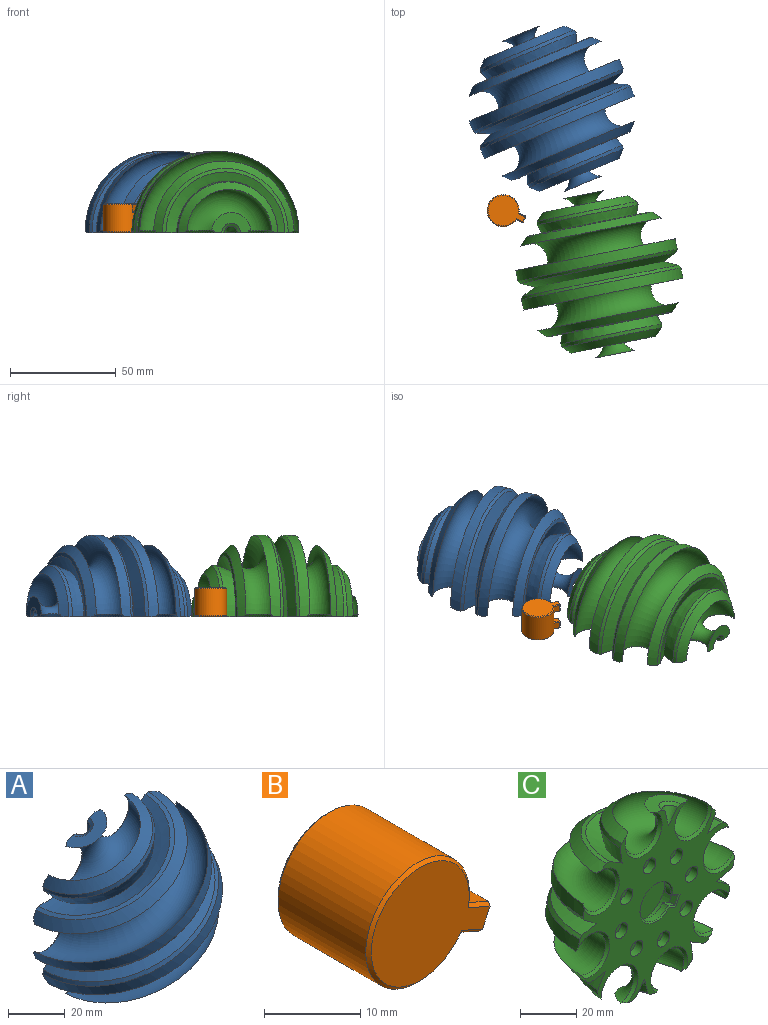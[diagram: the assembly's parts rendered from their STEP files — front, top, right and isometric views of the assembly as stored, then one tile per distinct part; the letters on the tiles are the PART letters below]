
ASSEMBLY  parts=3 mates=2
PART A: 64 faces, bbox 92.5x49.9x87.6 mm
  f0: torus R=12.63mm, axis (-0.38,0,0.92), area 20.6mm2, adj f1,f21,f22
  f1: cone r=3.5mm half-angle=24.8deg, axis (0.38,0,-0.92), area 0.6mm2, adj f0,f22,f59
  f2: plane 17.7x9.72mm, normal (0.38,0,-0.92), area 108.9mm2, adj f3,f22,f50,f51,f59
  f3: torus R=12.81mm, axis (-0.38,0,0.92), area 1353.3mm2, adj f2,f4,f50,f51
  f4: cone r=20.48mm half-angle=45deg, axis (-0.38,0,0.92), area 350.6mm2, adj f3,f22,f50,f51,f61
  f5: cone r=24.75mm half-angle=20.2deg, axis (0.38,0,-0.92), area 533.9mm2, adj f6,f22,f61
  f6: cone r=29.7mm half-angle=69.8deg, axis (0.38,0,-0.92), area 584.1mm2, adj f5,f22,f60
  f7: cone r=29.7mm half-angle=45deg, axis (-0.38,0,0.92), area 508mm2, adj f8,f22,f49,f52,f60
  f8: torus R=30.92mm, axis (-0.38,0,0.92), area 3393.7mm2, adj f7,f9,f49,f52
  f9: cylinder r=38.5mm len=73.07mm, axis (-0.38,0,0.92), area 608mm2, adj f8,f22,f49,f52,f63
  f10: cone r=38.5mm half-angle=65.2deg, axis (0.38,0,-0.92), area 790.5mm2, adj f11,f22,f63
  f11: cone r=38.5mm half-angle=65.2deg, axis (-0.38,0,0.92), area 790.5mm2, adj f10,f22,f62
  f12: cylinder r=38.5mm len=73.07mm, axis (-0.38,0,0.92), area 608mm2, adj f13,f22,f48,f53,f62
  f13: torus R=30.92mm, axis (-0.38,0,0.92), area 3395.4mm2, adj f12,f14,f48,f53
  f14: cone r=33.97mm half-angle=45deg, axis (0.38,0,-0.92), area 508mm2, adj f13,f22,f48,f53,f58
  f15: cone r=29.7mm half-angle=69.8deg, axis (-0.38,0,0.92), area 584.1mm2, adj f16,f22,f58
  f16: cone r=24.75mm half-angle=20.2deg, axis (-0.38,0,0.92), area 533.9mm2, adj f15,f22,f57
  f17: cone r=24.75mm half-angle=45deg, axis (0.38,0,-0.92), area 350.7mm2, adj f18,f22,f54,f55,f57
  f18: torus R=12.81mm, axis (-0.38,0,0.92), area 1355.2mm2, adj f17,f19,f54,f55
  f19: plane 17.7x9.72mm, normal (-0.38,0,0.92), area 108.9mm2, adj f18,f22,f54,f55,f56
  f20: cone r=3.5mm half-angle=24.8deg, axis (-0.38,0,0.92), area 35.5mm2, adj f22,f56
  f21: cone r=1.93mm half-angle=24.8deg, axis (0.38,0,-0.92), area 9.3mm2, adj f0,f22
  f22: plane 81.31x81.3mm, normal (0,1,0), area 2232.2mm2, adj f0,f1,f2,f4,f5,f6,f7,f9
  f23: cylinder r=3.15mm len=6.3mm, axis (0,1,0), area 66.3mm2, adj f22,f24
  f24: plane 6.3x6.3mm, normal (0,1,0), area 31.2mm2, adj f23
  f25: cylinder r=3.15mm len=6.3mm, axis (0,1,0), area 66.3mm2, adj f22,f26
  f26: plane 6.3x6.3mm, normal (0,1,0), area 31.2mm2, adj f25
  f27: cylinder r=3.15mm len=6.3mm, axis (0,1,0), area 66.3mm2, adj f22,f28
  f28: plane 6.3x6.3mm, normal (0,1,0), area 31.2mm2, adj f27
  f29: cylinder r=3.15mm len=6.3mm, axis (0,1,0), area 66.3mm2, adj f22,f30
  f30: plane 6.3x6.3mm, normal (0,1,0), area 31.2mm2, adj f29
  f31: cylinder r=3.15mm len=6.3mm, axis (0,1,0), area 66.3mm2, adj f22,f32
  f32: plane 6.3x6.3mm, normal (0,1,0), area 31.2mm2, adj f31
  f33: cylinder r=3.15mm len=6.3mm, axis (0,1,0), area 66.3mm2, adj f22,f34
  f34: plane 6.3x6.3mm, normal (0,1,0), area 31.2mm2, adj f33
  f35: cylinder r=3.15mm len=6.3mm, axis (0,1,0), area 66.3mm2, adj f22,f36
  f36: plane 6.3x6.3mm, normal (0,1,0), area 31.2mm2, adj f35
  f37: cylinder r=3.15mm len=6.3mm, axis (0,1,0), area 66.3mm2, adj f22,f38
  f38: plane 6.3x6.3mm, normal (0,1,0), area 31.2mm2, adj f37
  f39: plane 7.15x3.45mm, normal (-0.42,0,-0.91), area 11.2mm2, adj f22,f40,f42,f43,f44,f45,f47
  f40: cylinder r=7.8mm len=15.6mm, axis (0,1,0), area 105.7mm2, adj f39,f41,f44,f45
  f41: plane 3.29x2.85mm, normal (0.42,0,0.91), area 10.2mm2, adj f22,f40,f42,f44,f45
  f42: plane 7.15x3.64mm, normal (-0.91,0,0.42), area 14.3mm2, adj f22,f39,f41,f43,f46,f47
  f43: plane 22.71x22.71mm, normal (0,1,0), area 405.1mm2, adj f39,f42,f47
  f44: cone r=8.3mm half-angle=45deg, axis (0,1,0), area 32.9mm2, adj f22,f39,f40,f41
  f45: plane 22.71x22.71mm, normal (0,-1,0), area 199.5mm2, adj f39,f40,f41,f47
  f46: plane 3.02x1.39mm, normal (0,-1,0), area 0.3mm2, adj f42,f47
  f47: cylinder r=11.35mm len=22.71mm, axis (0,1,0), area 303.8mm2, adj f39,f42,f43,f45,f46
  f48: bspline ~18.61x18.6mm, area 55.9mm2, adj f12,f13,f14,f22
  f49: bspline ~18.57x17.08mm, area 55.8mm2, adj f7,f8,f9,f22
  f50: bspline ~18.69x18.61mm, area 57.5mm2, adj f2,f3,f4,f22
  f51: bspline ~18.66x17.09mm, area 57.5mm2, adj f2,f3,f4,f22
  f52: bspline ~18.51x18.5mm, area 55.9mm2, adj f7,f8,f9,f22
  f53: bspline ~18.5x15.69mm, area 55.9mm2, adj f12,f13,f14,f22
  f54: bspline ~18.69x18.61mm, area 57.5mm2, adj f17,f18,f19,f22
  f55: bspline ~18.66x17.09mm, area 57.5mm2, adj f17,f18,f19,f22
  f56: cone r=3.08mm half-angle=57.4deg, axis (-0.38,0,0.92), area 20.1mm2, adj f19,f20,f22
  f57: cone r=24.04mm half-angle=12.4deg, axis (0.38,0,-0.92), area 128.2mm2, adj f16,f17,f22
  f58: cone r=28.76mm half-angle=77.6deg, axis (0.38,0,-0.92), area 156.6mm2, adj f14,f15,f22
  f59: cone r=4.5mm half-angle=57.4deg, axis (0.38,0,-0.92), area 20.1mm2, adj f1,f2,f22
  f60: cone r=30.41mm half-angle=77.6deg, axis (-0.38,0,0.92), area 156.6mm2, adj f6,f7,f22
  f61: cone r=24.4mm half-angle=12.4deg, axis (-0.38,0,0.92), area 128.2mm2, adj f4,f5,f22
  f62: cone r=38.5mm half-angle=32.6deg, axis (-0.38,0,0.92), area 201.4mm2, adj f11,f12,f22
  f63: cone r=37.59mm half-angle=32.6deg, axis (0.38,0,-0.92), area 201.4mm2, adj f9,f10,f22
PART B: 37 faces, bbox 18.2x13.7x15.2 mm
  f0: cylinder r=7.6mm len=15.2mm, axis (0,1,0), area 591.6mm2, adj f4,f5,f6,f7,f9,f10,f11,f18
  f1: plane 17.45x14.4mm, normal (0,-1,0), area 171.6mm2, adj f24,f25,f26,f27
  f2: plane 17.45x14.4mm, normal (0,1,0), area 171.6mm2, adj f11,f12,f13,f14
  f3: plane 3.2x2.36mm, normal (0.91,0,-0.42), area 8.3mm2, adj f26,f31,f32,f36
  f4: plane 3.2x2.92mm, normal (0.42,0,0.91), area 10.3mm2, adj f0,f27,f32,f33
  f5: plane 3.2x2.78mm, normal (-0.42,0,-0.91), area 9.8mm2, adj f0,f25,f30,f31
  f6: plane 3.81x3.66mm, normal (0,1,0), area 7.7mm2, adj f0,f30,f33,f36
  f7: plane 3.2x2.92mm, normal (0.42,0,0.91), area 10.3mm2, adj f0,f13,f19,f20
  f8: plane 3.2x2.36mm, normal (0.91,0,-0.42), area 8.3mm2, adj f14,f17,f20,f23
  f9: plane 3.2x2.78mm, normal (-0.42,0,-0.91), area 9.8mm2, adj f0,f12,f17,f18
  f10: plane 3.81x3.66mm, normal (0,-1,0), area 7.7mm2, adj f0,f18,f19,f23
  f11: cone r=7.6mm half-angle=45deg, axis (0,-1,0), area 24.6mm2, adj f0,f2,f12,f13
  f12: plane 3.09x1.79mm, normal (-0.29,0.71,-0.64), area 1.8mm2, adj f2,f9,f11,f15
  f13: plane 3.37x1.71mm, normal (0.29,0.71,0.64), area 1.9mm2, adj f2,f7,f11,f16
  f14: plane 2.53x1.45mm, normal (0.64,0.71,-0.29), area 1.5mm2, adj f2,f8,f15,f16
  f15: plane 0.53x0.4mm, normal (0.28,0.58,-0.77), area 0.1mm2, adj f12,f14,f17
  f16: plane 0.53x0.4mm, normal (0.77,0.58,0.28), area 0.1mm2, adj f13,f14,f20
  f17: plane 3.2x0.53mm, normal (0.35,0,-0.94), area 1.8mm2, adj f8,f9,f15,f21
  f18: plane 2.94x1.61mm, normal (-0.29,-0.71,-0.64), area 1.7mm2, adj f0,f9,f10,f21
  f19: plane 2.99x1.7mm, normal (0.29,-0.71,0.64), area 1.8mm2, adj f0,f7,f10,f22
  f20: plane 3.2x0.53mm, normal (0.94,0,0.35), area 1.8mm2, adj f7,f8,f16,f22
  f21: plane 0.53x0.4mm, normal (0.28,-0.58,-0.77), area 0.1mm2, adj f17,f18,f23
  f22: plane 0.53x0.4mm, normal (0.77,-0.58,0.28), area 0.1mm2, adj f19,f20,f23
  f23: plane 2.53x1.45mm, normal (0.64,-0.71,-0.29), area 1.5mm2, adj f8,f10,f21,f22
  f24: cone r=7.2mm half-angle=45deg, axis (0,1,0), area 24.6mm2, adj f0,f1,f25,f27
  f25: plane 3.09x1.79mm, normal (-0.29,-0.71,-0.64), area 1.8mm2, adj f1,f5,f24,f28
  f26: plane 2.53x1.45mm, normal (0.64,-0.71,-0.29), area 1.5mm2, adj f1,f3,f28,f29
  f27: plane 3.37x1.71mm, normal (0.29,-0.71,0.64), area 1.9mm2, adj f1,f4,f24,f29
  f28: plane 0.53x0.4mm, normal (0.28,-0.58,-0.77), area 0.1mm2, adj f25,f26,f31
  f29: plane 0.53x0.4mm, normal (0.77,-0.58,0.28), area 0.1mm2, adj f26,f27,f32
  f30: plane 2.94x1.61mm, normal (-0.29,0.71,-0.64), area 1.7mm2, adj f0,f5,f6,f34
  f31: plane 3.2x0.53mm, normal (0.35,0,-0.94), area 1.8mm2, adj f3,f5,f28,f34
  f32: plane 3.2x0.53mm, normal (0.94,0,0.35), area 1.8mm2, adj f3,f4,f29,f35
  f33: plane 2.99x1.7mm, normal (0.29,0.71,0.64), area 1.8mm2, adj f0,f4,f6,f35
  f34: plane 0.53x0.4mm, normal (0.28,0.58,-0.77), area 0.1mm2, adj f30,f31,f36
  f35: plane 0.53x0.4mm, normal (0.77,0.58,0.28), area 0.1mm2, adj f32,f33,f36
  f36: plane 2.53x1.45mm, normal (0.64,0.71,-0.29), area 1.5mm2, adj f3,f6,f34,f35
PART C: 65 faces, bbox 92.5x46.8x87.3 mm
  f0: cone r=3.5mm half-angle=24.8deg, axis (-0.2,0,-0.98), area 35.5mm2, adj f1,f36
  f1: cone r=3.08mm half-angle=57.4deg, axis (-0.2,0,-0.98), area 20.1mm2, adj f0,f2,f36
  f2: plane 18.78x9.72mm, normal (-0.2,0,-0.98), area 108.9mm2, adj f1,f3,f34,f35,f36
  f3: bspline ~18.66x17.95mm, area 57.5mm2, adj f2,f4,f34,f36
  f4: cone r=20.48mm half-angle=45deg, axis (0.2,0,0.98), area 350.6mm2, adj f3,f5,f34,f35,f36
  f5: cone r=24.04mm half-angle=12.4deg, axis (0.2,0,0.98), area 128.2mm2, adj f4,f6,f36
  f6: cone r=24.75mm half-angle=20.2deg, axis (-0.2,0,-0.98), area 533.9mm2, adj f5,f7,f36
  f7: cone r=29.7mm half-angle=69.8deg, axis (-0.2,0,-0.98), area 584.1mm2, adj f6,f8,f36
  f8: cone r=28.76mm half-angle=77.6deg, axis (0.2,0,0.98), area 156.6mm2, adj f7,f9,f36
  f9: cone r=29.7mm half-angle=45deg, axis (0.2,0,0.98), area 508mm2, adj f8,f10,f32,f33,f36
  f10: bspline ~18.57x18.57mm, area 55.9mm2, adj f9,f11,f32,f36
  f11: cylinder r=38.5mm len=76.5mm, axis (-0.2,0,-0.98), area 607.9mm2, adj f10,f12,f32,f33,f36
  f12: cone r=38.5mm half-angle=32.6deg, axis (-0.2,0,-0.98), area 201.4mm2, adj f11,f13,f36
  f13: cone r=38.5mm half-angle=65.2deg, axis (-0.2,0,-0.98), area 790.5mm2, adj f12,f14,f36
  f14: cone r=38.5mm half-angle=65.2deg, axis (0.2,0,0.98), area 790.5mm2, adj f13,f15,f36
  f15: cone r=37.59mm half-angle=32.6deg, axis (0.2,0,0.98), area 201.4mm2, adj f14,f16,f36
  f16: cylinder r=38.5mm len=76.5mm, axis (-0.2,0,-0.98), area 608mm2, adj f15,f17,f30,f31,f36
  f17: bspline ~18.55x17.94mm, area 55.9mm2, adj f16,f18,f30,f36
  f18: cone r=33.97mm half-angle=45deg, axis (-0.2,0,-0.98), area 508mm2, adj f17,f19,f30,f31,f36
  f19: cone r=30.41mm half-angle=77.6deg, axis (-0.2,0,-0.98), area 156.6mm2, adj f18,f20,f36
  f20: cone r=29.7mm half-angle=69.8deg, axis (0.2,0,0.98), area 584.1mm2, adj f19,f21,f36
  f21: cone r=24.75mm half-angle=20.2deg, axis (0.2,0,0.98), area 533.9mm2, adj f20,f22,f36
  f22: cone r=24.4mm half-angle=12.4deg, axis (-0.2,0,-0.98), area 128.2mm2, adj f21,f23,f36
  f23: cone r=24.75mm half-angle=45deg, axis (-0.2,0,-0.98), area 350.7mm2, adj f22,f24,f28,f29,f36
  f24: bspline ~18.68x18.56mm, area 57.5mm2, adj f23,f25,f28,f36
  f25: plane 18.78x9.72mm, normal (0.2,0,0.98), area 108.9mm2, adj f24,f26,f28,f29,f36
  f26: cone r=4.5mm half-angle=57.4deg, axis (0.2,0,0.98), area 20.1mm2, adj f25,f27,f36
  f27: cone r=3.5mm half-angle=24.8deg, axis (0.2,0,0.98), area 14.8mm2, adj f26,f36
  f28: torus R=12.81mm, axis (-0.2,0,-0.98), area 1352.1mm2, adj f23,f24,f25,f29
  f29: bspline ~18.66x17.95mm, area 57.5mm2, adj f23,f25,f28,f36
  f30: torus R=30.92mm, axis (-0.2,0,-0.98), area 3393.7mm2, adj f16,f17,f18,f31
  f31: bspline ~18.57x18.57mm, area 55.9mm2, adj f16,f18,f30,f36
  f32: torus R=30.92mm, axis (-0.2,0,-0.98), area 3395.4mm2, adj f9,f10,f11,f33
  f33: bspline ~18.55x17.94mm, area 55.8mm2, adj f9,f11,f32,f36
  f34: torus R=12.81mm, axis (-0.2,0,-0.98), area 1355.2mm2, adj f2,f3,f4,f35
  f35: bspline ~18.68x18.57mm, area 57.5mm2, adj f2,f4,f34,f36
  f36: plane 82.86x82.82mm, normal (0,-1,0), area 2226.7mm2, adj f0,f1,f2,f3,f4,f5,f6,f7
  f37: cone r=3.5mm half-angle=24.8deg, axis (0.2,0,0.98), area 3mm2, adj f36
  f38: cylinder r=3.15mm len=6.3mm, axis (0,1,0), area 66.3mm2, adj f36,f39
  f39: plane 6.3x6.3mm, normal (0,-1,0), area 31.2mm2, adj f38
  f40: cylinder r=3.15mm len=6.3mm, axis (0,1,0), area 66.3mm2, adj f36,f41
  f41: plane 6.3x6.3mm, normal (0,-1,0), area 31.2mm2, adj f40
  f42: cylinder r=3.15mm len=6.3mm, axis (0,1,0), area 66.3mm2, adj f36,f43
  f43: plane 6.3x6.3mm, normal (0,-1,0), area 31.2mm2, adj f42
  f44: cylinder r=3.15mm len=6.3mm, axis (0,1,0), area 66.3mm2, adj f36,f45
  f45: plane 6.3x6.3mm, normal (0,-1,0), area 31.2mm2, adj f44
  f46: cylinder r=3.15mm len=6.3mm, axis (0,1,0), area 66.3mm2, adj f36,f47
  f47: plane 6.3x6.3mm, normal (0,-1,0), area 31.2mm2, adj f46
  f48: cylinder r=3.15mm len=6.3mm, axis (0,1,0), area 66.3mm2, adj f36,f49
  f49: plane 6.3x6.3mm, normal (0,-1,0), area 31.2mm2, adj f48
  f50: cylinder r=3.15mm len=6.3mm, axis (0,1,0), area 66.3mm2, adj f36,f51
  f51: plane 6.3x6.3mm, normal (0,-1,0), area 31.2mm2, adj f50
  f52: cylinder r=3.15mm len=6.3mm, axis (0,1,0), area 66.3mm2, adj f36,f53
  f53: plane 6.3x6.3mm, normal (0,-1,0), area 31.2mm2, adj f52
  f54: plane 4.12x1.9mm, normal (-0.29,-0.71,-0.64), area 2.7mm2, adj f36,f55,f62,f64
  f55: plane 3.44x2.55mm, normal (-0.42,0,-0.91), area 9.7mm2, adj f54,f56,f60,f61
  f56: plane 22.94x22.94mm, normal (0,1,0), area 208.2mm2, adj f55,f57,f59,f60,f61
  f57: cylinder r=11.47mm len=22.94mm, axis (0,-1,0), area 295.5mm2, adj f56,f58
  f58: plane 22.94x22.94mm, normal (0,-1,0), area 413.5mm2, adj f57
  f59: plane 3.28x2.55mm, normal (0.42,0,0.91), area 9.2mm2, adj f56,f60,f61,f63
  f60: cylinder r=7.8mm len=15.6mm, axis (0,1,0), area 114.6mm2, adj f55,f56,f59,f62
  f61: plane 3.64x2.55mm, normal (-0.91,0,0.42), area 10.2mm2, adj f55,f56,f59,f64
  f62: cone r=7.8mm half-angle=45deg, axis (0,-1,0), area 32.5mm2, adj f36,f54,f60,f63
  f63: plane 3.54x2.18mm, normal (0.29,-0.71,0.64), area 2.6mm2, adj f36,f59,f62,f64
  f64: plane 4.54x2.33mm, normal (-0.64,-0.71,0.29), area 3.2mm2, adj f36,f54,f61,f63
PLACE A rot(axis=(-1,0,0),90deg) t=(-4.25,92.07,-81.55)mm
PLACE B rot(axis=(-1,0,0),90deg) t=(-27.22,43.79,-74.7)mm
PLACE C rot(axis=(1,0,0),90deg) t=(18.32,13.58,-81.55)mm
MATE planar C.f60 <-> A.f40  axis (0,0,-1) through (18.32,13.58,-81.55)mm
MATE planar B.f2 <-> A.f40  axis (0,0,-1) through (-26.8,43.61,-81.55)mm
